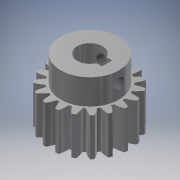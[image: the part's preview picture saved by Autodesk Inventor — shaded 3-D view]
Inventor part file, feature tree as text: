
AUTODESK INVENTOR PART (.ipt)
format: ipt  version: 2019 (Build 230136000, 136)  size: 282,624 bytes
history: native  units: mm (DEFAULTED — no unit token found)
features: sketch x7, extrude x6, plane x5, other x5
ambient origin geometry x8: Origin, YZ Plane, XZ Plane, XY Plane, X Axis, Y Axis, Z Axis, Center Point
bodies: Solid1 (feature_tree)
feature tree (23):
  extrude  "Extrusion1"  Depth=15.0mm TaperAngle=0.0deg
  plane  "Work Plane2"
  plane  "Work Plane8"
  plane  "Work Plane9"
  other  "正齒輪"
  extrude  "擠出2"  Depth=10.0mm TaperAngle=0.0deg
  extrude  "擠出3"  Depth=10.0mm
  extrude  "擠出4"  Depth=10.0mm TaperAngle=0.0deg
  plane  "工作平面11"
  extrude  "擠出5"  TaperAngle=0.0deg  [1 undecoded]
  plane  "工作平面12"
  extrude  "擠出6"  TaperAngle=0.0deg  [1 undecoded]
  other  "螺紋1"
  other  "螺紋2"
  sketch  "Sketch1"  dims[d0=31.5mm d1=15.0mm d2=0.0mm]
  sketch  "Sketch2"  dims[d3=28.5mm d4=10.0mm d5=0.0mm d16=57.0mm d17=0.0mm d34=1.65347mm d39=0.0mm d41=0.0mm d43=57.0mm d46=57.0mm d47=0.0mm d48=0.0mm d49=23.0mm d50=10.0mm d51=0.0mm d52=10.0mm d53=14.0mm d54=0.0mm d57=2.0mm d58=11.8mm d59=14.0mm d60=0.0mm d61=4.5mm d62=4.0mm d63=14.0mm d64=0.0mm d65=4.5mm d66=4.0mm d67=0.0mm d68=0.0mm d69=10.0mm d70=0.0mm d71=10.0mm d72=0.0mm]
  other  "Srf1"
  sketch  "草圖3"
  sketch  "草圖4"
  sketch  "草圖5"
  sketch  "草圖6"
  sketch  "草圖7"
  other  "節圓直徑"
note: 2 required parameter values undecoded (feature->parameter linkage not recoverable at this tier; creation-order binding heuristic only, values carry confidence <= 0.55)
